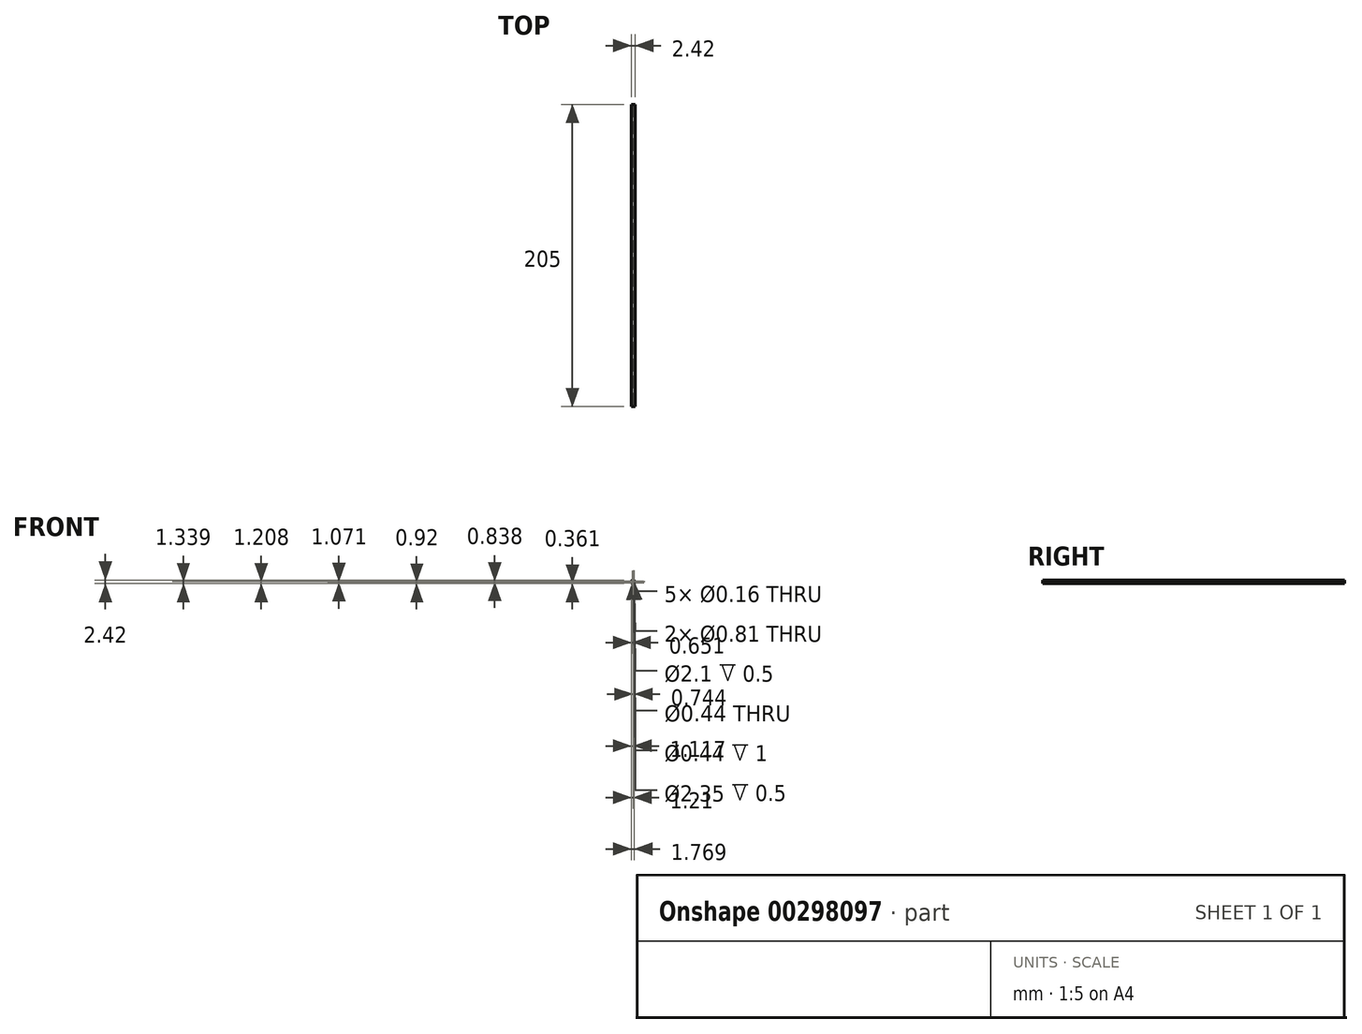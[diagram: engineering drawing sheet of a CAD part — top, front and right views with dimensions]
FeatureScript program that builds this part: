
annotation { "Feature Type Name" : "Feature", "Feature Type Description" : "" }
export const myFeature = defineFeature(function(context is Context, id is Id, definition is map)
    precondition{}
    {
        {
            var Q0;
            Q0=qCreatedBy(makeId("Front.planeOp"),FACE);
            var sketch = newSketch(context, id + "F0", { "sketchPlane" : qUnion([Q0])});
            skCircle(sketch, "E0", {"center": v(0, 0) * mm, "radius": 0.4 * mm});
            skCircle(sketch, "E1", {"center": v(-0.1, -0.56) * mm, "radius": 0.08 * mm});
            skCircle(sketch, "E2", {"center": v(0.1, -0.56) * mm, "radius": 0.08 * mm});
            skCircle(sketch, "E3", {"center": v(0, 0.84) * mm, "radius": 0.4 * mm});
            skCircle(sketch, "E4", {"center": v(0.65, 0.51) * mm, "radius": 0.08 * mm});
            skCircle(sketch, "E5", {"center": v(0.65, 0.32) * mm, "radius": 0.08 * mm});
            skCircle(sketch, "E6", {"center": v(0.47, 0.42) * mm, "radius": 0.08 * mm});
            skCircle(sketch, "E7", {"center": v(0.56, 0.42) * mm, "radius": 0.22 * mm});
            skEllipse(sketch, "E8", {"center": v(0, -0.56) * mm, "majorRadius": 0.23 * mm, "minorRadius": 0.11 * mm, "majorAxis": v(1, 0)});
            skCircle(sketch, "E9.MirrorC", {"center": v(-0.56, 0.42) * mm, "radius": 0.22 * mm});
            skCircle(sketch, "E10.MirrorC", {"center": v(-0.65, 0.51) * mm, "radius": 0.08 * mm});
            skCircle(sketch, "E11.MirrorC", {"center": v(-0.47, 0.42) * mm, "radius": 0.08 * mm});
            skCircle(sketch, "E12.MirrorC", {"center": v(-0.65, 0.32) * mm, "radius": 0.08 * mm});
            skPoint(sketch, "E13", {"position": v(0, 1.24) * mm});
            skPoint(sketch, "E14", {"position": v(0, -0.67) * mm});
            skPoint(sketch, "E15", {"position": v(0, 0.29) * mm});
            skCircle(sketch, "E16", {"center": v(0, 0.29) * mm, "radius": 1.2 * mm});
            skCircle(sketch, "E17", {"center": v(0, 0.29) * mm, "radius": 1.05 * mm});
            skSolve(sketch);
        }
        {
            var Q0;
            Q0 = qSketchRegion(id + "F0", true);
            var Q1;
            Q1=makeQuery(id+"F0.imprint","IMPRINT",FACE,{"disambiguationData":[TD([[makeQuery(id+"F0.imprint","IMPRINT",EDGE,{"derivedFrom":sQuery(id+"F0.wireOp",EDGE,"E0")}),-1.0]])]});
            var Q2;
            Q2=makeQuery(id+"F0.imprint","IMPRINT",FACE,{"disambiguationData":[TD([[makeQuery(id+"F0.imprint","IMPRINT",EDGE,{"derivedFrom":sQuery(id+"F0.wireOp",EDGE,"E9.MirrorC")}),-1.0]])]});
            var Q3;
            Q3=makeQuery(id+"F0.imprint","IMPRINT",FACE,{"disambiguationData":[TD([[makeQuery(id+"F0.imprint","IMPRINT",EDGE,{"derivedFrom":sQuery(id+"F0.wireOp",EDGE,"E4")}),-1.0]])]});
            var Q4;
            Q4=makeQuery(id+"F0.imprint","IMPRINT",FACE,{"disambiguationData":[TD([[makeQuery(id+"F0.imprint","IMPRINT",EDGE,{"derivedFrom":sQuery(id+"F0.wireOp",EDGE,"E16")}),1.0]])]});
            var Q5;
            Q5=makeQuery(id+"F0.imprint","IMPRINT",FACE,{"disambiguationData":[TD([[makeQuery(id+"F0.imprint","IMPRINT",EDGE,{"derivedFrom":sQuery(id+"F0.wireOp",EDGE,"E1")}),-1.0]])]});
            extrude(context, id + "F1", {"entities" : qUnion([Q0, Q1, Q2, Q3, Q4, Q5]), "depth" : 205 * mm});
        }
        {
            var Q0;
            Q0=makeQuery(id+"F1.opExtrude","CAP_FACE",FACE,{"disambiguationData":[OSD([sQuery(id+"F0.wireOp",EDGE,"E0"),sQuery(id+"F0.wireOp",EDGE,"E1"),sQuery(id+"F0.wireOp",EDGE,"E2"),sQuery(id+"F0.wireOp",EDGE,"E3"),sQuery(id+"F0.wireOp",EDGE,"E4"),sQuery(id+"F0.wireOp",EDGE,"E5"),sQuery(id+"F0.wireOp",EDGE,"E6"),sQuery(id+"F0.wireOp",EDGE,"E10.MirrorC"),sQuery(id+"F0.wireOp",EDGE,"E11.MirrorC"),sQuery(id+"F0.wireOp",EDGE,"E12.MirrorC"),sQuery(id+"F0.wireOp",EDGE,"E16")])],"isStart":false});
            var sketch = newSketch(context, id + "F2", { "sketchPlane" : qUnion([Q0])});
            skCircle(sketch, "E18.0.0", {"center": v(0, 0.29) * mm, "radius": 1.2 * mm});
            skCircle(sketch, "E19", {"center": v(0, 0.29) * mm, "radius": 1.05 * mm});
            skSolve(sketch);
        }
        {
            var Q0;
            Q0=makeQuery(id+"F2.imprint","IMPRINT",FACE,{"disambiguationData":[TD([[makeQuery(id+"F2.imprint","IMPRINT",EDGE,{"derivedFrom":sQuery(id+"F2.wireOp",EDGE,"E19")}),1.0]])]});
            extrude(context, id + "F3", {"entities" : qUnion([Q0]), "operationType" : NewBodyOperationType.REMOVE, "oppositeDirection" : true, "depth" : 1 * mm});
        }
        {
            var Q0;
            Q0=makeQuery(id+"F3.boolean.opBoolean","COPY",FACE,{"derivedFrom":makeQuery(id+"F3.opExtrude","CAP_FACE",FACE,{"disambiguationData":[OSD([sQuery(id+"F0.wireOp",EDGE,"E0"),sQuery(id+"F0.wireOp",EDGE,"E1"),sQuery(id+"F0.wireOp",EDGE,"E2"),sQuery(id+"F0.wireOp",EDGE,"E3"),sQuery(id+"F0.wireOp",EDGE,"E4"),sQuery(id+"F0.wireOp",EDGE,"E5"),sQuery(id+"F0.wireOp",EDGE,"E6"),sQuery(id+"F0.wireOp",EDGE,"E10.MirrorC"),sQuery(id+"F0.wireOp",EDGE,"E11.MirrorC"),sQuery(id+"F0.wireOp",EDGE,"E12.MirrorC"),sQuery(id+"F2.wireOp",EDGE,"E19")])],"isStart":false})});
            var sketch = newSketch(context, id + "F4", { "sketchPlane" : qUnion([Q0])});
            skPoint(sketch, "E20", {"position": v(0.56, 0.42) * mm});
            skPoint(sketch, "E21", {"position": v(-0.56, 0.42) * mm});
            skCircle(sketch, "E22.0.0", {"center": v(0, 0.29) * mm, "radius": 1.05 * mm});
            skCircle(sketch, "E23", {"center": v(0.56, 0.42) * mm, "radius": 0.22 * mm});
            skCircle(sketch, "E24", {"center": v(-0.56, 0.42) * mm, "radius": 0.22 * mm});
            skCircle(sketch, "E25.0", {"center": v(0.1, -0.56) * mm, "radius": 0.08 * mm});
            skCircle(sketch, "E26.0", {"center": v(-0.1, -0.56) * mm, "radius": 0.08 * mm});
            skLineSegment(sketch, "E27", {"start": v(-0.1, -0.56) * mm, "end": v(0.1, -0.56) * mm});
            skEllipse(sketch, "E28", {"center": v(0, -0.56) * mm, "majorRadius": 0.23 * mm, "minorRadius": 0.1 * mm, "majorAxis": v(1, 0)});
            skSolve(sketch);
        }
        {
            var Q0;
            Q0=makeQuery(id+"F4.imprint","IMPRINT",FACE,{"disambiguationData":[TD([[makeQuery(id+"F4.imprint","IMPRINT",EDGE,{"derivedFrom":sQuery(id+"F4.wireOp",EDGE,"E24")}),1.0]])]});
            var Q1;
            Q1=makeQuery(id+"F4.imprint","IMPRINT",FACE,{"disambiguationData":[TD([[makeQuery(id+"F4.imprint","IMPRINT",EDGE,{"derivedFrom":sQuery(id+"F4.wireOp",EDGE,"E23")}),1.0]])]});
            var Q2;
            Q2=makeQuery(id+"F4.imprint","IMPRINT",FACE,{"disambiguationData":[TD([[makeQuery(id+"F4.imprint","IMPRINT",EDGE,{"derivedFrom":sQuery(id+"F4.wireOp",EDGE,"E25.0")}),-1.0]])]});
            extrude(context, id + "F5", {"entities" : qUnion([Q0, Q1, Q2]), "operationType" : NewBodyOperationType.REMOVE, "oppositeDirection" : true, "depth" : 1 * mm});
        }
        {
            var Q0;
            Q0=makeQuery(id+"F1.opExtrude","CAP_FACE",FACE,{"disambiguationData":[OSD([sQuery(id+"F0.wireOp",EDGE,"E0"),sQuery(id+"F0.wireOp",EDGE,"E1"),sQuery(id+"F0.wireOp",EDGE,"E2"),sQuery(id+"F0.wireOp",EDGE,"E3"),sQuery(id+"F0.wireOp",EDGE,"E4"),sQuery(id+"F0.wireOp",EDGE,"E5"),sQuery(id+"F0.wireOp",EDGE,"E6"),sQuery(id+"F0.wireOp",EDGE,"E10.MirrorC"),sQuery(id+"F0.wireOp",EDGE,"E11.MirrorC"),sQuery(id+"F0.wireOp",EDGE,"E12.MirrorC"),sQuery(id+"F0.wireOp",EDGE,"E16")])],"isStart":false});
            var sketch = newSketch(context, id + "F6", { "sketchPlane" : qUnion([Q0])});
            skCircle(sketch, "E29.0.0", {"center": v(0, 0.29) * mm, "radius": 1.2 * mm});
            skCircle(sketch, "E30", {"center": v(0, 0.29) * mm, "radius": 1.18 * mm});
            skSolve(sketch);
        }
        {
            var Q0;
            Q0=makeQuery(id+"F6.imprint","IMPRINT",FACE,{"disambiguationData":[TD([[makeQuery(id+"F6.imprint","IMPRINT",EDGE,{"derivedFrom":sQuery(id+"F6.wireOp",EDGE,"E30")}),1.0]])]});
            extrude(context, id + "F7", {"entities" : qUnion([Q0]), "operationType" : NewBodyOperationType.REMOVE, "oppositeDirection" : true, "depth" : 0.5 * mm});
        }
    });
